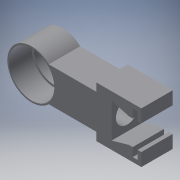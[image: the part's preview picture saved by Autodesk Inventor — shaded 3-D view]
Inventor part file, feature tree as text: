
AUTODESK INVENTOR PART (.ipt)
format: ipt  version: 2016 (Build 200138000, 138)  size: 254,464 bytes
history: native  units: mm
features: extrude x10, sketch x10, projected_geometry x2, reference x1
ambient origin geometry x8: Origin, YZ Plane, XZ Plane, XY Plane, X Axis, Y Axis, Z Axis, Center Point
bodies: Solid1 (feature_tree)
feature tree (23):
  extrude  "Extrusion1"  Depth=7.0mm
  extrude  "Extrusion2"  Depth=15.0mm
  extrude  "Extrusion3"  Depth=0.25mm
  extrude  "Extrusion4"  Depth=14.5mm TaperAngle=0.0deg
  extrude  "Extrusion5"  Depth=3.75mm
  extrude  "Extrusion6"  Depth=21.5mm
  extrude  "Extrusion7"  Depth=20.0mm
  extrude  "Extrusion9"  Depth=19.0mm
  extrude  "Extrusion10"  Depth=10.5mm
  extrude  "Extrusion11"  Depth=1.0mm TaperAngle=0.0deg
  sketch  "Sketch1"  dims[d0=23.495mm d1=7.0mm]
  sketch  "Sketch2"  dims[d2=4.0mm d3=2.0mm d4=6.0mm d5=2.0mm d6=4.0mm d7=2.0mm d8=6.0mm d9=2.0mm d10=15.0mm d11=15.0mm d12=0.25mm]
  sketch  "Sketch3"  dims[d13=0.25mm d14=0.25mm]
  sketch  "Sketch4"  dims[d15=0.25mm d16=14.5mm d17=0.0mm]
  sketch  "Sketch5"  dims[d18=3.749998mm d19=3.75mm]
  sketch  "Sketch6"  dims[d20=30.0mm d21=0.0mm d22=21.5mm]
  sketch  "Sketch7"  dims[d23=14.5mm d24=0.0mm d25=20.0mm]
  sketch  "Sketch9"  dims[d26=10.5mm d27=0.0mm d28=19.0mm]
  sketch  "Sketch10"  dims[d29=10.5mm d30=0.0mm d31=10.5mm]
  projected_geometry  "Projected Loop1"
  projected_geometry  "Projected Loop2"
  sketch  "Sketch11"  dims[d32=40.0mm d33=0.0mm d34=1.0mm d35=0.0mm d39=3.0mm d40=3.0mm d41=3.0mm d42=3.0mm d43=20.0mm d44=3.0mm d45=0.0mm d46=3.0mm d47=0.0mm d48=5.75mm d49=0.0mm d50=21.5mm]
  reference  "Reference1"
